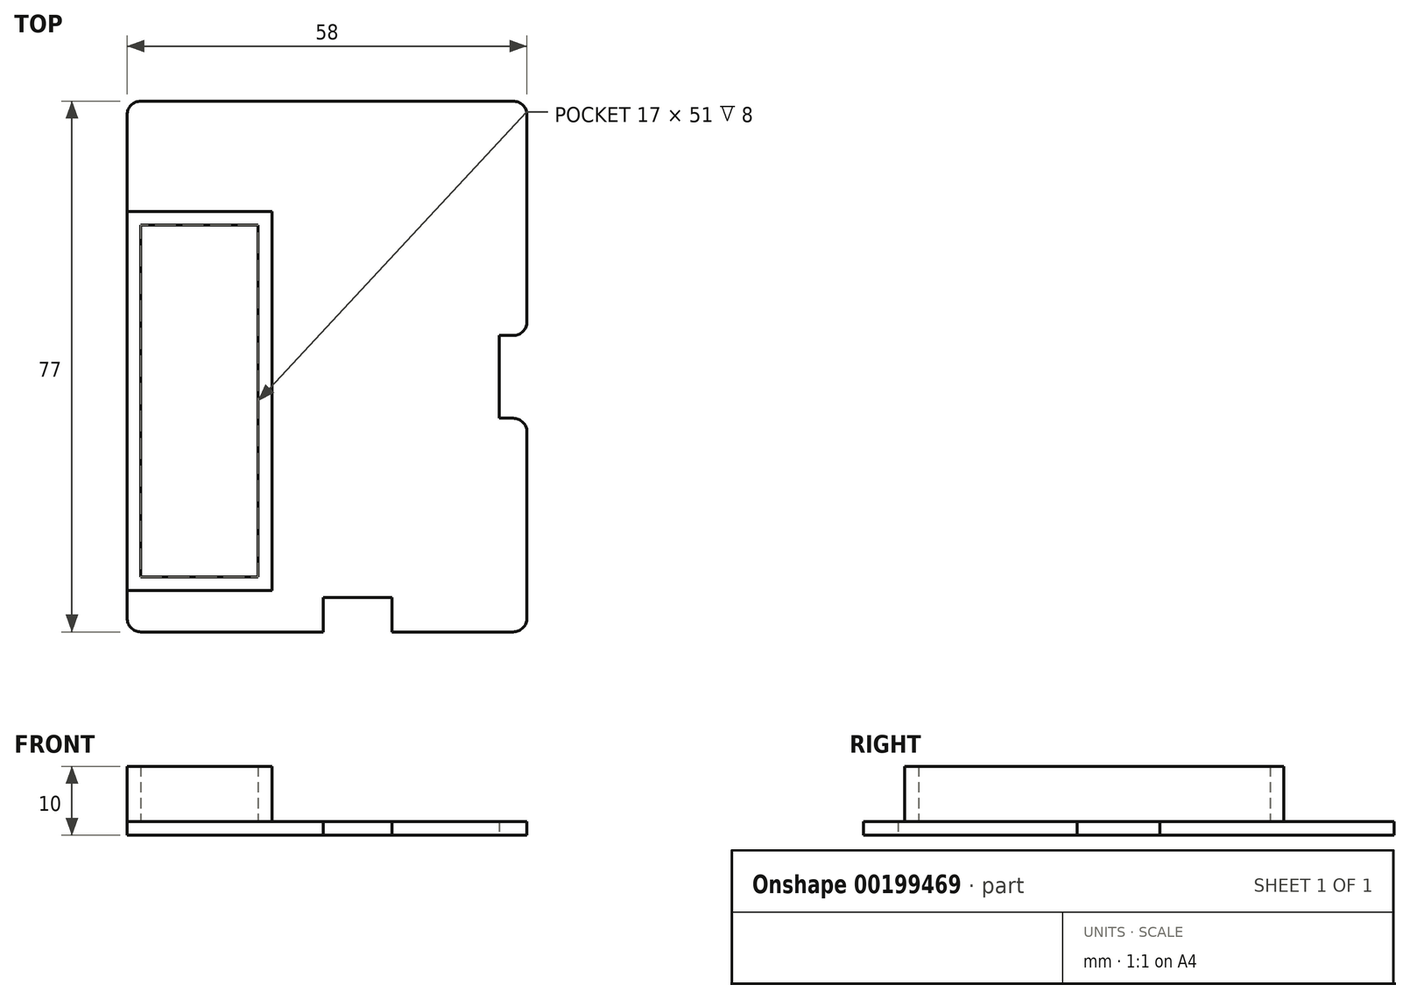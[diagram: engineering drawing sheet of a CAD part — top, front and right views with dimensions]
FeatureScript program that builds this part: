
annotation { "Feature Type Name" : "Feature", "Feature Type Description" : "" }
export const myFeature = defineFeature(function(context is Context, id is Id, definition is map)
    precondition{}
    {
        {
            var Q0;
            Q0=qCreatedBy(makeId("Top.planeOp"),FACE);
            var sketch = newSketch(context, id + "F0", { "sketchPlane" : qUnion([Q0])});
            skLineSegment(sketch, "E0.bottom", {"start": v(-3.6, 39.42) * mm, "end": v(54.4, 39.42) * mm});
            skLineSegment(sketch, "E0.top", {"start": v(-3.6, -37.58) * mm, "end": v(54.4, -37.58) * mm});
            skLineSegment(sketch, "E0.left", {"start": v(-3.6, 39.42) * mm, "end": v(-3.6, -37.58) * mm});
            skLineSegment(sketch, "E0.right", {"start": v(54.4, 39.42) * mm, "end": v(54.4, -37.58) * mm});
            skLineSegment(sketch, "E1.top", {"start": v(-3.6, 39.42) * mm, "end": v(18.4, 39.42) * mm});
            skLineSegment(sketch, "E1.left", {"start": v(-3.6, 17.42) * mm, "end": v(-3.6, 39.42) * mm});
            skLineSegment(sketch, "E2.bottom", {"start": v(54.4, -6.58) * mm, "end": v(50.4, -6.58) * mm});
            skLineSegment(sketch, "E2.top", {"start": v(54.4, 5.42) * mm, "end": v(50.4, 5.42) * mm});
            skLineSegment(sketch, "E2.left", {"start": v(54.4, -6.58) * mm, "end": v(54.4, 5.42) * mm});
            skLineSegment(sketch, "E2.right", {"start": v(50.4, -6.58) * mm, "end": v(50.4, 5.42) * mm});
            skLineSegment(sketch, "E3.bottom", {"start": v(-3.6, -31.58) * mm, "end": v(17.4, -31.58) * mm});
            skLineSegment(sketch, "E3.top", {"start": v(-3.6, 23.42) * mm, "end": v(17.4, 23.42) * mm});
            skLineSegment(sketch, "E3.left", {"start": v(-3.6, -31.58) * mm, "end": v(-3.6, 23.42) * mm});
            skLineSegment(sketch, "E3.right", {"start": v(17.4, -31.58) * mm, "end": v(17.4, 23.42) * mm});
            skLineSegment(sketch, "E4.top", {"start": v(54.4, 39.42) * mm, "end": v(32.4, 39.42) * mm});
            skLineSegment(sketch, "E4.left", {"start": v(54.4, 17.42) * mm, "end": v(54.4, 39.42) * mm});
            skLineSegment(sketch, "E5.bottom", {"start": v(34.84, -37.58) * mm, "end": v(24.84, -37.58) * mm});
            skLineSegment(sketch, "E5.top", {"start": v(34.84, -32.58) * mm, "end": v(24.84, -32.58) * mm});
            skLineSegment(sketch, "E5.left", {"start": v(34.84, -37.58) * mm, "end": v(34.84, -32.58) * mm});
            skLineSegment(sketch, "E5.right", {"start": v(24.84, -37.58) * mm, "end": v(24.84, -32.58) * mm});
            skSolve(sketch);
        }
        {
            var Q0;
            {var subQ6=sQuery(id+"F0.wireOp",EDGE,"E0.bottom");Q0=makeQuery(id+"F0.imprint","IMPRINT",FACE,{"disambiguationData":[TD([[makeQuery(id+"F0.imprint","IMPRINT",EDGE,{"derivedFrom":subQ6}),-1.0]])]});}
            var Q1;
            Q1=makeQuery(id+"F0.imprint","IMPRINT",FACE,{"disambiguationData":[TD([[makeQuery(id+"F0.imprint","IMPRINT",EDGE,{"derivedFrom":sQuery(id+"F0.wireOp",EDGE,"E3.bottom")}),1.0]])]});
            extrude(context, id + "F1", {"entities" : qUnion([Q0, Q1]), "depth" : 2 * mm});
        }
        {
            var Q0;
            Q0=makeQuery(id+"F0.imprint","IMPRINT",FACE,{"disambiguationData":[TD([[makeQuery(id+"F0.imprint","IMPRINT",EDGE,{"derivedFrom":sQuery(id+"F0.wireOp",EDGE,"E3.bottom")}),1.0]])]});
            extrude(context, id + "F2", {"entities" : qUnion([Q0]), "operationType" : NewBodyOperationType.ADD, "depth" : 10 * mm});
        }
        {
            var Q0;
            Q0=makeQuery(id+"F2.opExtrude","CAP_FACE",FACE,{"disambiguationData":[OSD([sQuery(id+"F0.wireOp",EDGE,"E3.bottom"),sQuery(id+"F0.wireOp",EDGE,"E3.top"),sQuery(id+"F0.wireOp",EDGE,"E3.left"),sQuery(id+"F0.wireOp",EDGE,"E3.right")])],"isStart":false});
            shell(context, id + "F3", {"entities" : qUnion([Q0]), "thickness" : 2 * mm});
        }
        {
            var Q0;
            Q0=makeQuery(id+"F1.opExtrude","SWEPT_EDGE",EDGE,{"disambiguationData":[OSD([sQuery(id+"F0.wireOp",EDGE,"E0.bottom"),sQuery(id+"F0.wireOp",EDGE,"E0.right")])]});
            var Q1;
            Q1=makeQuery(id+"F1.opExtrude","SWEPT_EDGE",EDGE,{"disambiguationData":[OSD([sQuery(id+"F0.wireOp",EDGE,"E0.bottom"),sQuery(id+"F0.wireOp",EDGE,"E1.top"),sQuery(id+"F0.wireOp",EDGE,"E1.right")])]});
            var Q2;
            Q2=makeQuery(id+"F1.opExtrude","SWEPT_EDGE",EDGE,{"disambiguationData":[OSD([sQuery(id+"F0.wireOp",EDGE,"E0.left"),sQuery(id+"F0.wireOp",EDGE,"E1.bottom"),sQuery(id+"F0.wireOp",EDGE,"E1.left")])]});
            var Q3;
            Q3=makeQuery(id+"F1.opExtrude","SWEPT_EDGE",EDGE,{"disambiguationData":[OSD([sQuery(id+"F0.wireOp",EDGE,"E0.top"),sQuery(id+"F0.wireOp",EDGE,"E0.right")])]});
            var Q4;
            Q4=makeQuery(id+"F1.opExtrude","SWEPT_EDGE",EDGE,{"disambiguationData":[OSD([sQuery(id+"F0.wireOp",EDGE,"E0.top"),sQuery(id+"F0.wireOp",EDGE,"E0.left")])]});
            var Q5;
            Q5=makeQuery(id+"F1.opExtrude","SWEPT_EDGE",EDGE,{"disambiguationData":[OSD([sQuery(id+"F0.wireOp",EDGE,"E0.bottom"),sQuery(id+"F0.wireOp",EDGE,"E4.top"),sQuery(id+"F0.wireOp",EDGE,"E4.right")])]});
            var Q6;
            Q6=makeQuery(id+"F1.opExtrude","SWEPT_EDGE",EDGE,{"disambiguationData":[OSD([sQuery(id+"F0.wireOp",EDGE,"E0.right"),sQuery(id+"F0.wireOp",EDGE,"E4.bottom"),sQuery(id+"F0.wireOp",EDGE,"E4.left")])]});
            fillet(context, id + "F4", {"entities" : qUnion([Q0, Q1, Q2, Q3, Q4, Q5, Q6]), "radius" : 2 * mm, "tangentPropagation" : true, "allowEdgeOverflow" : false});
        }
    });
